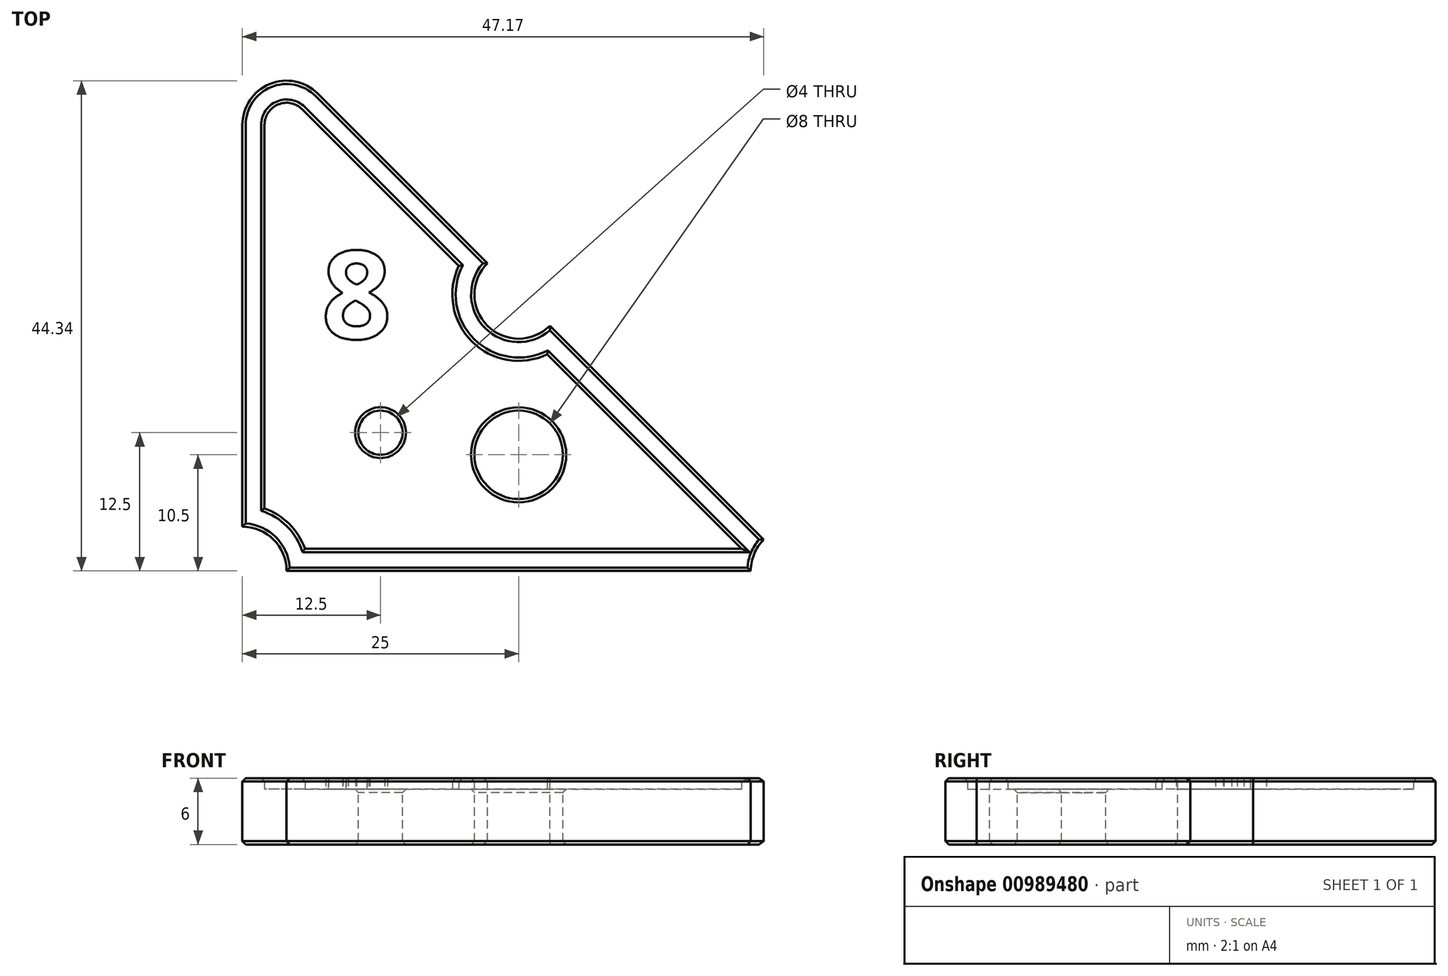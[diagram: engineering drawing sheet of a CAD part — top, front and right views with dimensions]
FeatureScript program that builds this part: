
annotation { "Feature Type Name" : "Feature", "Feature Type Description" : "" }
export const myFeature = defineFeature(function(context is Context, id is Id, definition is map)
    precondition{}
    {
        {
            var Q0;
            Q0=qCreatedBy(makeId("Top.planeOp"),FACE);
            var sketch = newSketch(context, id + "F0", { "sketchPlane" : qUnion([Q0])});
            skLineSegment(sketch, "E0", {"start": v(-25, 25) * mm, "end": v(-25, -25) * mm});
            skLineSegment(sketch, "E1", {"start": v(-25, -25) * mm, "end": v(25, -25) * mm});
            skLineSegment(sketch, "E2", {"start": v(25, -25) * mm, "end": v(-25, 25) * mm});
            skPoint(sketch, "E3", {"position": v(0, 0) * mm});
            skCircle(sketch, "E4", {"center": v(-25, -25) * mm, "radius": 4 * mm});
            skCircle(sketch, "E5", {"center": v(25, -25) * mm, "radius": 4 * mm});
            skCircle(sketch, "E6", {"center": v(0, 0) * mm, "radius": 4 * mm});
            skArc(sketch, "E7", {"start": v(-18.17, 18.17) * mm, "mid": v(-22.53, 19.04) * mm, "end": v(-25, 15.34) * mm});
            skCircle(sketch, "E8", {"center": v(-12.5, -12.5) * mm, "radius": 2 * mm});
            skLineSegment(sketch, "E9", {"start": v(0, 0) * mm, "end": v(-25, -25) * mm, "construction": true});
            skCircle(sketch, "E10", {"center": v(0, -14.5) * mm, "radius": 4 * mm});
            skLineSegment(sketch, "E11", {"start": v(0, -4) * mm, "end": v(0, -25) * mm, "construction": true});
            skPoint(sketch, "E11.startSnap0", {"position": v(0, -25) * mm});
            skLineSegment(sketch, "E12", {"start": v(-4, 4) * mm, "end": v(-4, -6.56) * mm, "construction": true});
            skLineSegment(sketch, "E13", {"start": v(-4, 0) * mm, "end": v(-25, 0) * mm, "construction": true});
            skText(sketch, "E14", { "text": "8", "fontName": "OpenSans-Bold.ttf"});
            skPoint(sketch, "E15", {"position": v(-14.5, 0) * mm});
            const initialGuessF0  = {"E14": [-0.01784, -0.004, 1, 0, 0.008]};
            skSetInitialGuess(sketch, initialGuessF0);
            skSolve(sketch);
        }
        {
            var Q0;
            {var subQ5=sQuery(id+"F0.wireOp",EDGE,"E7");Q0=makeQuery(id+"F0.imprint","IMPRINT",FACE,{"disambiguationData":[TD([[makeQuery(id+"F0.imprint","IMPRINT",EDGE,{"derivedFrom":subQ5}),1.0]])]});}
            var Q1;
            Q1=makeQuery(id+"F0.imprint","IMPRINT",FACE,{"disambiguationData":[TD([[makeQuery(id+"F0.imprint","IMPRINT",EDGE,{"derivedFrom":sQuery(id+"F0.wireOp",EDGE,"E14.sketch_text.stroke-0")}),-1.0]])]});
            var Q2;
            Q2=makeQuery(id+"F0.imprint","IMPRINT",FACE,{"disambiguationData":[TD([[makeQuery(id+"F0.imprint","IMPRINT",EDGE,{"derivedFrom":sQuery(id+"F0.wireOp",EDGE,"E14.sketch_text.stroke-23")}),1.0]])]});
            var Q3;
            Q3=makeQuery(id+"F0.imprint","IMPRINT",FACE,{"disambiguationData":[TD([[makeQuery(id+"F0.imprint","IMPRINT",EDGE,{"derivedFrom":sQuery(id+"F0.wireOp",EDGE,"E14.sketch_text.stroke-16")}),1.0]])]});
            extrude(context, id + "F1", {"entities" : qUnion([Q0, Q1, Q2, Q3]), "oppositeDirection" : true, "depth" : 5 * mm, "offsetDistance" : 25 * mm});
        }
        {
            var Q0;
            Q0=makeQuery(id+"F1.opExtrude","CAP_FACE",FACE,{"disambiguationData":[OSD([sQuery(id+"F0.wireOp",EDGE,"E0"),sQuery(id+"F0.wireOp",EDGE,"E1"),sQuery(id+"F0.wireOp",EDGE,"E2"),sQuery(id+"F0.wireOp",EDGE,"E4"),sQuery(id+"F0.wireOp",EDGE,"E5"),sQuery(id+"F0.wireOp",EDGE,"E6"),sQuery(id+"F0.wireOp",EDGE,"E7"),sQuery(id+"F0.wireOp",EDGE,"E8"),sQuery(id+"F0.wireOp",EDGE,"E10")])],"isStart":true});
            var sketch = newSketch(context, id + "F2", { "sketchPlane" : qUnion([Q0])});
            skLineSegment(sketch, "E16.0", {"start": v(20.17, -23) * mm, "end": v(2.59, -5.41) * mm});
            skLineSegment(sketch, "E16.1", {"start": v(-19.34, -23) * mm, "end": v(20.17, -23) * mm});
            skLineSegment(sketch, "E16.2", {"start": v(-5.41, 2.59) * mm, "end": v(-19.59, 16.76) * mm});
            skArc(sketch, "E16.3", {"start": v(-19.59, 16.76) * mm, "mid": v(-21.77, 17.2) * mm, "end": v(-23, 15.34) * mm});
            skLineSegment(sketch, "E16.4", {"start": v(-23, 15.34) * mm, "end": v(-23, -19.34) * mm});
            skArc(sketch, "E16.5", {"start": v(2.59, -5.41) * mm, "mid": v(-4.24, -4.24) * mm, "end": v(-5.41, 2.59) * mm});
            skArc(sketch, "E16.6", {"start": v(-23, -19.34) * mm, "mid": v(-20.76, -20.76) * mm, "end": v(-19.34, -23) * mm});
            skSolve(sketch);
        }
        {
            var Q0;
            Q0=makeQuery(id+"F0.imprint","IMPRINT",FACE,{"disambiguationData":[TD([[makeQuery(id+"F0.imprint","IMPRINT",EDGE,{"derivedFrom":sQuery(id+"F0.wireOp",EDGE,"E14.sketch_text.stroke-0")}),-1.0]])]});
            var Q1;
            Q1=makeQuery(id+"F2.imprint","IMPRINT",FACE,{"disambiguationData":[TD([[makeQuery(id+"F2.imprint","IMPRINT",EDGE,{"derivedFrom":sQuery(id+"F2.wireOp",EDGE,"E16.0")}),-1.0]])]});
            extrude(context, id + "F3", {"entities" : qUnion([Q0, Q1]), "operationType" : NewBodyOperationType.ADD, "depth" : 1 * mm, "offsetDistance" : 25 * mm});
        }
        {
            var Q0;
            Q0=makeQuery(id+"F3.opExtrude","CAP_FACE",FACE,{"disambiguationData":[OSD([sQuery(id+"F0.wireOp",EDGE,"E0"),sQuery(id+"F0.wireOp",EDGE,"E1"),sQuery(id+"F0.wireOp",EDGE,"E2"),sQuery(id+"F0.wireOp",EDGE,"E4"),sQuery(id+"F0.wireOp",EDGE,"E5"),sQuery(id+"F0.wireOp",EDGE,"E6"),sQuery(id+"F0.wireOp",EDGE,"E7"),sQuery(id+"F2.wireOp",EDGE,"E16.0"),sQuery(id+"F2.wireOp",EDGE,"E16.1"),sQuery(id+"F2.wireOp",EDGE,"E16.2"),sQuery(id+"F2.wireOp",EDGE,"E16.3"),sQuery(id+"F2.wireOp",EDGE,"E16.4"),sQuery(id+"F2.wireOp",EDGE,"E16.5"),sQuery(id+"F2.wireOp",EDGE,"E16.6")])],"isStart":false});
            var Q1;
            Q1=makeQuery(id+"F1.opExtrude","CAP_EDGE",EDGE,{"disambiguationData":[OSD([sQuery(id+"F0.wireOp",EDGE,"E8")])],"isStart":true});
            var Q2;
            Q2=makeQuery(id+"F1.opExtrude","CAP_EDGE",EDGE,{"disambiguationData":[OSD([sQuery(id+"F0.wireOp",EDGE,"E10")])],"isStart":true});
            var Q3;
            Q3=makeQuery(id+"F1.opExtrude","CAP_FACE",FACE,{"disambiguationData":[OSD([sQuery(id+"F0.wireOp",EDGE,"E0"),sQuery(id+"F0.wireOp",EDGE,"E1"),sQuery(id+"F0.wireOp",EDGE,"E2"),sQuery(id+"F0.wireOp",EDGE,"E4"),sQuery(id+"F0.wireOp",EDGE,"E5"),sQuery(id+"F0.wireOp",EDGE,"E6"),sQuery(id+"F0.wireOp",EDGE,"E7"),sQuery(id+"F0.wireOp",EDGE,"E8"),sQuery(id+"F0.wireOp",EDGE,"E10")])],"isStart":false});
            chamfer(context, id + "F4", {"entities" : qUnion([Q0, Q1, Q2, Q3]), "width" : 0.3 * mm, "tangentPropagation" : true});
        }
    });
